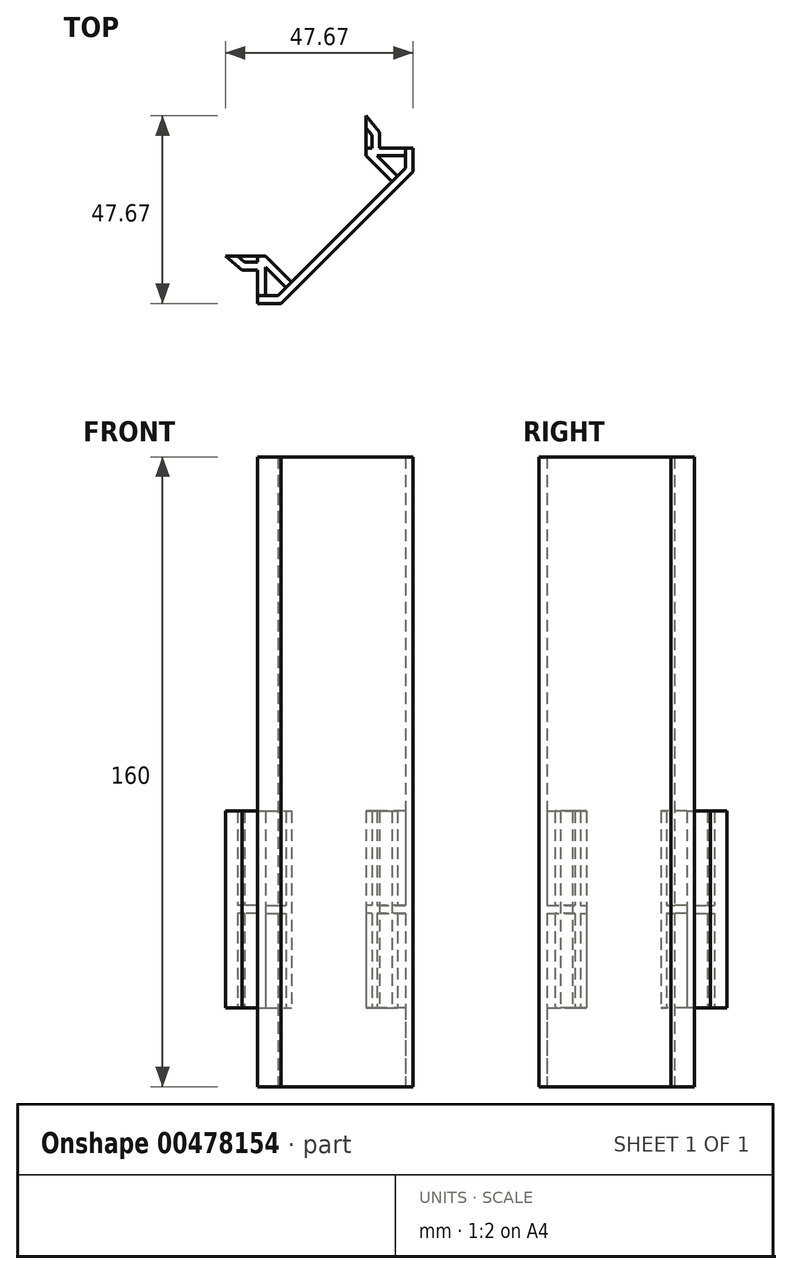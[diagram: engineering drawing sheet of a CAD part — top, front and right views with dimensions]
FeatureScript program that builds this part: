
annotation { "Feature Type Name" : "Feature", "Feature Type Description" : "" }
export const myFeature = defineFeature(function(context is Context, id is Id, definition is map)
    precondition{}
    {
        {
            var Q0;
            Q0=qCreatedBy(makeId("Top.planeOp"),FACE);
            var sketch = newSketch(context, id + "F0", { "sketchPlane" : qUnion([Q0])});
            skLineSegment(sketch, "E0", {"start": v(-68.1, 0) * mm, "end": v(72.16, 0) * mm, "construction": true});
            skLineSegment(sketch, "E1", {"start": v(0, 70.28) * mm, "end": v(0, -61.88) * mm, "construction": true});
            skLineSegment(sketch, "E2.bottom", {"start": v(-19.75, 19.75) * mm, "end": v(19.75, 19.75) * mm, "construction": true});
            skLineSegment(sketch, "E2.top", {"start": v(-19.75, -19.75) * mm, "end": v(19.75, -19.75) * mm, "construction": true});
            skLineSegment(sketch, "E2.left", {"start": v(-19.75, 19.75) * mm, "end": v(-19.75, -19.75) * mm, "construction": true});
            skLineSegment(sketch, "E2.right", {"start": v(19.75, 19.75) * mm, "end": v(19.75, -19.75) * mm, "construction": true});
            skLineSegment(sketch, "E3", {"start": v(-19.75, -19.75) * mm, "end": v(-13.75, -19.75) * mm});
            skLineSegment(sketch, "E4", {"start": v(19.75, 19.75) * mm, "end": v(19.75, 13.75) * mm});
            skLineSegment(sketch, "E5", {"start": v(-13.75, -19.75) * mm, "end": v(19.75, 13.75) * mm});
            skLineSegment(sketch, "E6.0", {"start": v(-19.75, -17.75) * mm, "end": v(-14.58, -17.75) * mm});
            skLineSegment(sketch, "E6.1", {"start": v(-14.58, -17.75) * mm, "end": v(17.75, 14.58) * mm});
            skLineSegment(sketch, "E6.2", {"start": v(17.75, 19.75) * mm, "end": v(17.75, 14.58) * mm});
            skLineSegment(sketch, "E7", {"start": v(-19.75, -19.75) * mm, "end": v(-19.75, -17.75) * mm});
            skLineSegment(sketch, "E8", {"start": v(19.75, 19.75) * mm, "end": v(17.75, 19.75) * mm});
            skSolve(sketch);
        }
        {
            var Q0;
            Q0 = qSketchRegion(id + "F0", true);
            extrude(context, id + "F1", {"entities" : qUnion([Q0]), "depth" : 20 * mm});
        }
        {
            var Q0;
            Q0=makeQuery(id+"F1.opExtrude","CAP_FACE",FACE,{"disambiguationData":[OSD([sQuery(id+"F0.wireOp",EDGE,"E3"),sQuery(id+"F0.wireOp",EDGE,"E4"),sQuery(id+"F0.wireOp",EDGE,"E5"),sQuery(id+"F0.wireOp",EDGE,"E6.0"),sQuery(id+"F0.wireOp",EDGE,"E6.1"),sQuery(id+"F0.wireOp",EDGE,"E6.2"),sQuery(id+"F0.wireOp",EDGE,"E7"),sQuery(id+"F0.wireOp",EDGE,"E8")])],"isStart":false});
            var sketch = newSketch(context, id + "F2", { "sketchPlane" : qUnion([Q0])});
            skLineSegment(sketch, "E9.1", {"start": v(-13.75, -19.75) * mm, "end": v(19.75, 13.75) * mm});
            skLineSegment(sketch, "E9.2", {"start": v(19.75, 19.75) * mm, "end": v(19.75, 13.75) * mm});
            skLineSegment(sketch, "E10", {"start": v(19.75, 19.75) * mm, "end": v(11.25, 19.75) * mm});
            skLineSegment(sketch, "E11", {"start": v(17.75, 17.75) * mm, "end": v(17.75, 14.58) * mm});
            skLineSegment(sketch, "E12", {"start": v(17.75, 14.58) * mm, "end": v(15.75, 12.58) * mm});
            skLineSegment(sketch, "E13.left", {"start": v(11.25, 19.75) * mm, "end": v(11.25, 23.75) * mm});
            skLineSegment(sketch, "E14", {"start": v(7.75, 17.75) * mm, "end": v(7.75, 19.75) * mm});
            skLineSegment(sketch, "E15", {"start": v(11.25, 23.75) * mm, "end": v(7.75, 27.92) * mm});
            skLineSegment(sketch, "E16", {"start": v(7.75, 17.75) * mm, "end": v(14.34, 11.16) * mm});
            skLineSegment(sketch, "E17.0", {"start": v(10.58, 17.75) * mm, "end": v(15.75, 12.58) * mm});
            skLineSegment(sketch, "E17.1", {"start": v(17.75, 17.75) * mm, "end": v(10.58, 17.75) * mm});
            skLineSegment(sketch, "E18.trimOffspring", {"start": v(14.34, 11.16) * mm, "end": v(-11.16, -14.34) * mm});
            skLineSegment(sketch, "E19.0", {"start": v(9.25, 19.75) * mm, "end": v(9.25, 23.02) * mm});
            skLineSegment(sketch, "E20.0", {"start": v(9.25, 23.02) * mm, "end": v(7.75, 24.8) * mm});
            skLineSegment(sketch, "E21", {"start": v(9.25, 19.75) * mm, "end": v(7.75, 19.75) * mm});
            skLineSegment(sketch, "E22.trimOffspring", {"start": v(7.75, 24.8) * mm, "end": v(7.75, 27.92) * mm});
            skLineSegment(sketch, "E23", {"start": v(0, 0) * mm, "end": v(3, -3) * mm, "construction": true});
            skLineSegment(sketch, "E24.MirrorCS", {"start": v(-19.75, -9.25) * mm, "end": v(-19.75, -7.75) * mm});
            skLineSegment(sketch, "E25.MirrorCS", {"start": v(-19.75, -9.25) * mm, "end": v(-23.02, -9.25) * mm});
            skLineSegment(sketch, "E26.MirrorCS", {"start": v(-17.75, -7.75) * mm, "end": v(-19.75, -7.75) * mm});
            skLineSegment(sketch, "E27.MirrorCS", {"start": v(-19.75, -11.25) * mm, "end": v(-23.75, -11.25) * mm});
            skLineSegment(sketch, "E28.MirrorCS", {"start": v(-17.75, -10.58) * mm, "end": v(-12.58, -15.75) * mm});
            skLineSegment(sketch, "E29.MirrorCS", {"start": v(-24.8, -7.75) * mm, "end": v(-27.92, -7.75) * mm});
            skLineSegment(sketch, "E30.MirrorCS", {"start": v(-19.75, -19.75) * mm, "end": v(-13.75, -19.75) * mm});
            skLineSegment(sketch, "E31.MirrorCS", {"start": v(-17.75, -7.75) * mm, "end": v(-11.16, -14.34) * mm});
            skLineSegment(sketch, "E32.MirrorCS", {"start": v(-14.58, -17.75) * mm, "end": v(-12.58, -15.75) * mm});
            skLineSegment(sketch, "E33.MirrorCS", {"start": v(-23.75, -11.25) * mm, "end": v(-27.92, -7.75) * mm});
            skLineSegment(sketch, "E34.MirrorCS", {"start": v(-17.75, -17.75) * mm, "end": v(-14.58, -17.75) * mm});
            skLineSegment(sketch, "E35.MirrorCS", {"start": v(-23.02, -9.25) * mm, "end": v(-24.8, -7.75) * mm});
            skLineSegment(sketch, "E36.MirrorCS", {"start": v(-19.75, -19.75) * mm, "end": v(-19.75, -11.25) * mm});
            skLineSegment(sketch, "E37.MirrorCS", {"start": v(-17.75, -17.75) * mm, "end": v(-17.75, -10.58) * mm});
            skLineSegment(sketch, "E38.trimOffspring", {"start": v(-12.58, -15.75) * mm, "end": v(-14.58, -17.75) * mm});
            skSolve(sketch);
        }
        {
            var Q0;
            Q0 = qSketchRegion(id + "F2", true);
            extrude(context, id + "F3", {"entities" : qUnion([Q0]), "operationType" : NewBodyOperationType.ADD, "depth" : 50 * mm});
        }
        {
            var Q0;
            Q0=makeQuery(id+"F3.opExtrude","CAP_FACE",FACE,{"disambiguationData":[OSD([sQuery(id+"F2.wireOp",EDGE,"18LkW5at-QDhS-aThv-tLml-cvOMEycPL9la"),sQuery(id+"F2.wireOp",EDGE,"E9.0"),sQuery(id+"F2.wireOp",EDGE,"E9.1"),sQuery(id+"F2.wireOp",EDGE,"E9.2"),sQuery(id+"F2.wireOp",EDGE,"E10"),sQuery(id+"F2.wireOp",EDGE,"E11"),sQuery(id+"F2.wireOp",EDGE,"E12"),sQuery(id+"F2.wireOp",EDGE,"gG7GE99v-zfpN-SBz3-vrGv-1yJCzINz42Ef"),sQuery(id+"F2.wireOp",EDGE,"UVh0vROw-WSek-6lxM-BEad-8BDBskrnTNki"),sQuery(id+"F2.wireOp",EDGE,"I0wHJKti-MazQ-Kak2-dpeP-lC7VClrsx2uq"),sQuery(id+"F2.wireOp",EDGE,"xpxs7AxX-igCE-9d4T-wt1V-guV83atNUd22"),sQuery(id+"F2.wireOp",EDGE,"PK7llsSc-NEYg-9CMv-nXlP-JqZKifBTAgQ1"),sQuery(id+"F2.wireOp",EDGE,"E13.top"),sQuery(id+"F2.wireOp",EDGE,"E13.left"),sQuery(id+"F2.wireOp",EDGE,"E13.right"),sQuery(id+"F2.wireOp",EDGE,"klJwY84u-2a2g-KLa0-gFfR-2CacjcHoM4EU")])],"isStart":false});
            var sketch = newSketch(context, id + "F4", { "sketchPlane" : qUnion([Q0])});
            skLineSegment(sketch, "E39.0", {"start": v(19.75, 19.75) * mm, "end": v(19.75, 13.75) * mm});
            skLineSegment(sketch, "E39.1.0", {"start": v(19.75, 19.75) * mm, "end": v(19.75, 13.75) * mm});
            skLineSegment(sketch, "E39.1.1", {"start": v(19.75, 13.75) * mm, "end": v(-13.75, -19.75) * mm});
            skLineSegment(sketch, "E39.1.2", {"start": v(-13.75, -19.75) * mm, "end": v(-19.75, -19.75) * mm});
            skLineSegment(sketch, "E39.1.3", {"start": v(-19.75, -19.75) * mm, "end": v(-19.75, -17.75) * mm});
            skLineSegment(sketch, "E39.1.4", {"start": v(-19.75, -17.75) * mm, "end": v(-14.58, -17.75) * mm});
            skLineSegment(sketch, "E39.1.5", {"start": v(-14.58, -17.75) * mm, "end": v(17.75, 14.58) * mm});
            skLineSegment(sketch, "E39.1.6", {"start": v(17.75, 14.58) * mm, "end": v(17.75, 19.75) * mm});
            skLineSegment(sketch, "E39.1.7", {"start": v(17.75, 19.75) * mm, "end": v(19.75, 19.75) * mm});
            skSolve(sketch);
        }
        {
            var Q0;
            Q0 = qSketchRegion(id + "F4", true);
            extrude(context, id + "F5", {"entities" : qUnion([Q0]), "operationType" : NewBodyOperationType.ADD, "depth" : 90 * mm});
        }
        {
            var Q0;
            {var subQ0=sQuery(id+"F2.wireOp",EDGE,"E28.MirrorCS");var subQ1=sQuery(id+"F2.wireOp",EDGE,"E27.MirrorCS");var subQ2=sQuery(id+"F2.wireOp",EDGE,"E26.MirrorCS");var subQ3=sQuery(id+"F2.wireOp",EDGE,"E25.MirrorCS");var subQ4=sQuery(id+"F2.wireOp",EDGE,"E18.trimOffspring");var subQ5=sQuery(id+"F2.wireOp",EDGE,"E31.MirrorCS");var subQ6=sQuery(id+"F2.wireOp",EDGE,"E24.MirrorCS");var subQ7=sQuery(id+"F2.wireOp",EDGE,"E34.MirrorCS");var subQ8=sQuery(id+"F2.wireOp",EDGE,"E12");var subQ9=sQuery(id+"F2.wireOp",EDGE,"E36.MirrorCS");var subQ10=sQuery(id+"F2.wireOp",EDGE,"E29.MirrorCS");var subQ11=sQuery(id+"F2.wireOp",EDGE,"E33.MirrorCS");var subQ12=sQuery(id+"F2.wireOp",EDGE,"E35.MirrorCS");var subQ13=sQuery(id+"F2.wireOp",EDGE,"E37.MirrorCS");var subQ14=sQuery(id+"F2.wireOp",EDGE,"E38.trimOffspring");Q0=makeQuery(id+"F5.boolean.opBoolean","SPLIT",FACE,{"disambiguationData":[TD([makeQuery(id+"F1.opExtrude","SWEPT_FACE",FACE,{"disambiguationData":[OSD([sQuery(id+"F0.wireOp",EDGE,"E6.0")])]})])],"derivedFrom":makeQuery(id+"F3.opExtrude","CAP_FACE",FACE,{"disambiguationData":[OSD([sQuery(id+"F2.wireOp",EDGE,"E9.1"),sQuery(id+"F2.wireOp",EDGE,"E9.2"),sQuery(id+"F2.wireOp",EDGE,"E10"),sQuery(id+"F2.wireOp",EDGE,"E11"),subQ8,sQuery(id+"F2.wireOp",EDGE,"E13.left"),sQuery(id+"F2.wireOp",EDGE,"E14"),sQuery(id+"F2.wireOp",EDGE,"E15"),sQuery(id+"F2.wireOp",EDGE,"E16"),sQuery(id+"F2.wireOp",EDGE,"E17.0"),sQuery(id+"F2.wireOp",EDGE,"E17.1"),subQ4,sQuery(id+"F2.wireOp",EDGE,"E19.0"),sQuery(id+"F2.wireOp",EDGE,"E20.0"),sQuery(id+"F2.wireOp",EDGE,"E21"),sQuery(id+"F2.wireOp",EDGE,"E22.trimOffspring"),subQ6,subQ3,subQ2,subQ1,subQ0,subQ10,sQuery(id+"F2.wireOp",EDGE,"E30.MirrorCS"),subQ5,subQ11,subQ7,subQ12,subQ9,subQ13,subQ14])],"isStart":false})});}
            var Q1;
            {var subQ0=sQuery(id+"F2.wireOp",EDGE,"E28.MirrorCS");var subQ1=sQuery(id+"F2.wireOp",EDGE,"E27.MirrorCS");var subQ2=sQuery(id+"F2.wireOp",EDGE,"E26.MirrorCS");var subQ3=sQuery(id+"F2.wireOp",EDGE,"E25.MirrorCS");var subQ4=sQuery(id+"F2.wireOp",EDGE,"E18.trimOffspring");var subQ5=sQuery(id+"F2.wireOp",EDGE,"E31.MirrorCS");var subQ6=sQuery(id+"F2.wireOp",EDGE,"E24.MirrorCS");var subQ7=sQuery(id+"F2.wireOp",EDGE,"E34.MirrorCS");var subQ8=sQuery(id+"F2.wireOp",EDGE,"E12");var subQ9=sQuery(id+"F2.wireOp",EDGE,"E36.MirrorCS");var subQ10=sQuery(id+"F2.wireOp",EDGE,"E29.MirrorCS");var subQ11=sQuery(id+"F2.wireOp",EDGE,"E33.MirrorCS");var subQ12=sQuery(id+"F2.wireOp",EDGE,"E35.MirrorCS");var subQ13=sQuery(id+"F2.wireOp",EDGE,"E37.MirrorCS");var subQ14=sQuery(id+"F2.wireOp",EDGE,"E38.trimOffspring");Q1=makeQuery(id+"F3.boolean.opBoolean","SPLIT",FACE,{"disambiguationData":[TD([makeQuery(id+"F1.opExtrude","SWEPT_FACE",FACE,{"disambiguationData":[OSD([sQuery(id+"F0.wireOp",EDGE,"E6.0")])]})])],"derivedFrom":makeQuery(id+"F3.opExtrude","CAP_FACE",FACE,{"disambiguationData":[OSD([sQuery(id+"F2.wireOp",EDGE,"E9.1"),sQuery(id+"F2.wireOp",EDGE,"E9.2"),sQuery(id+"F2.wireOp",EDGE,"E10"),sQuery(id+"F2.wireOp",EDGE,"E11"),subQ8,sQuery(id+"F2.wireOp",EDGE,"E13.left"),sQuery(id+"F2.wireOp",EDGE,"E14"),sQuery(id+"F2.wireOp",EDGE,"E15"),sQuery(id+"F2.wireOp",EDGE,"E16"),sQuery(id+"F2.wireOp",EDGE,"E17.0"),sQuery(id+"F2.wireOp",EDGE,"E17.1"),subQ4,sQuery(id+"F2.wireOp",EDGE,"E19.0"),sQuery(id+"F2.wireOp",EDGE,"E20.0"),sQuery(id+"F2.wireOp",EDGE,"E21"),sQuery(id+"F2.wireOp",EDGE,"E22.trimOffspring"),subQ6,subQ3,subQ2,subQ1,subQ0,subQ10,sQuery(id+"F2.wireOp",EDGE,"E30.MirrorCS"),subQ5,subQ11,subQ7,subQ12,subQ9,subQ13,subQ14])],"isStart":true})});}
            cPlane(context, id + "F6", {"entities" : qUnion([Q0, Q1]), "cplaneType" : CPlaneType.MID_PLANE, "offset" : 25 * mm, "width" : 150 * mm, "height" : 150 * mm});
        }
        {
            var Q0;
            Q0=qCreatedBy(id+"F6.planeOp",FACE);
            var sketch = newSketch(context, id + "F7", { "sketchPlane" : qUnion([Q0])});
            skLineSegment(sketch, "E40.0", {"start": v(-19.75, -9.25) * mm, "end": v(-19.75, -7.75) * mm});
            skLineSegment(sketch, "E41.0", {"start": v(-19.75, -9.25) * mm, "end": v(-23.02, -9.25) * mm});
            skLineSegment(sketch, "E41.1", {"start": v(-23.02, -9.25) * mm, "end": v(-24.8, -7.75) * mm});
            skLineSegment(sketch, "E42", {"start": v(-19.75, -7.75) * mm, "end": v(-24.8, -7.75) * mm});
            skLineSegment(sketch, "E43.0", {"start": v(9.25, 19.75) * mm, "end": v(9.25, 23.02) * mm});
            skLineSegment(sketch, "E43.1", {"start": v(9.25, 19.75) * mm, "end": v(7.75, 19.75) * mm});
            skLineSegment(sketch, "E43.2", {"start": v(9.25, 23.02) * mm, "end": v(7.75, 24.8) * mm});
            skLineSegment(sketch, "E44", {"start": v(7.75, 19.75) * mm, "end": v(7.75, 24.8) * mm});
            skLineSegment(sketch, "E45.0", {"start": v(17.75, 17.75) * mm, "end": v(10.58, 17.75) * mm});
            skLineSegment(sketch, "E45.1", {"start": v(10.58, 17.75) * mm, "end": v(15.75, 12.58) * mm});
            skLineSegment(sketch, "E45.2", {"start": v(-17.75, -10.58) * mm, "end": v(-12.58, -15.75) * mm});
            skLineSegment(sketch, "E45.3", {"start": v(-17.75, -17.75) * mm, "end": v(-17.75, -10.58) * mm});
            skLineSegment(sketch, "E46.0", {"start": v(17.75, 17.75) * mm, "end": v(17.75, 14.58) * mm});
            skLineSegment(sketch, "E46.1", {"start": v(-14.58, -17.75) * mm, "end": v(-12.58, -15.75) * mm});
            skLineSegment(sketch, "E46.2", {"start": v(-17.75, -17.75) * mm, "end": v(-14.58, -17.75) * mm});
            skPoint(sketch, "E47.orphan", {"position": v(17.75, 19.75) * mm});
            skLineSegment(sketch, "E48.trimOffspring", {"start": v(15.75, 12.58) * mm, "end": v(17.75, 14.58) * mm});
            skPoint(sketch, "E49.orphan", {"position": v(-19.75, -17.75) * mm});
            skSolve(sketch);
        }
        {
            var Q0;
            Q0 = qSketchRegion(id + "F7", true);
            extrude(context, id + "F8", {"entities" : qUnion([Q0]), "operationType" : NewBodyOperationType.ADD, "depth" : 2 * mm, "symmetric" : true});
        }
    });
